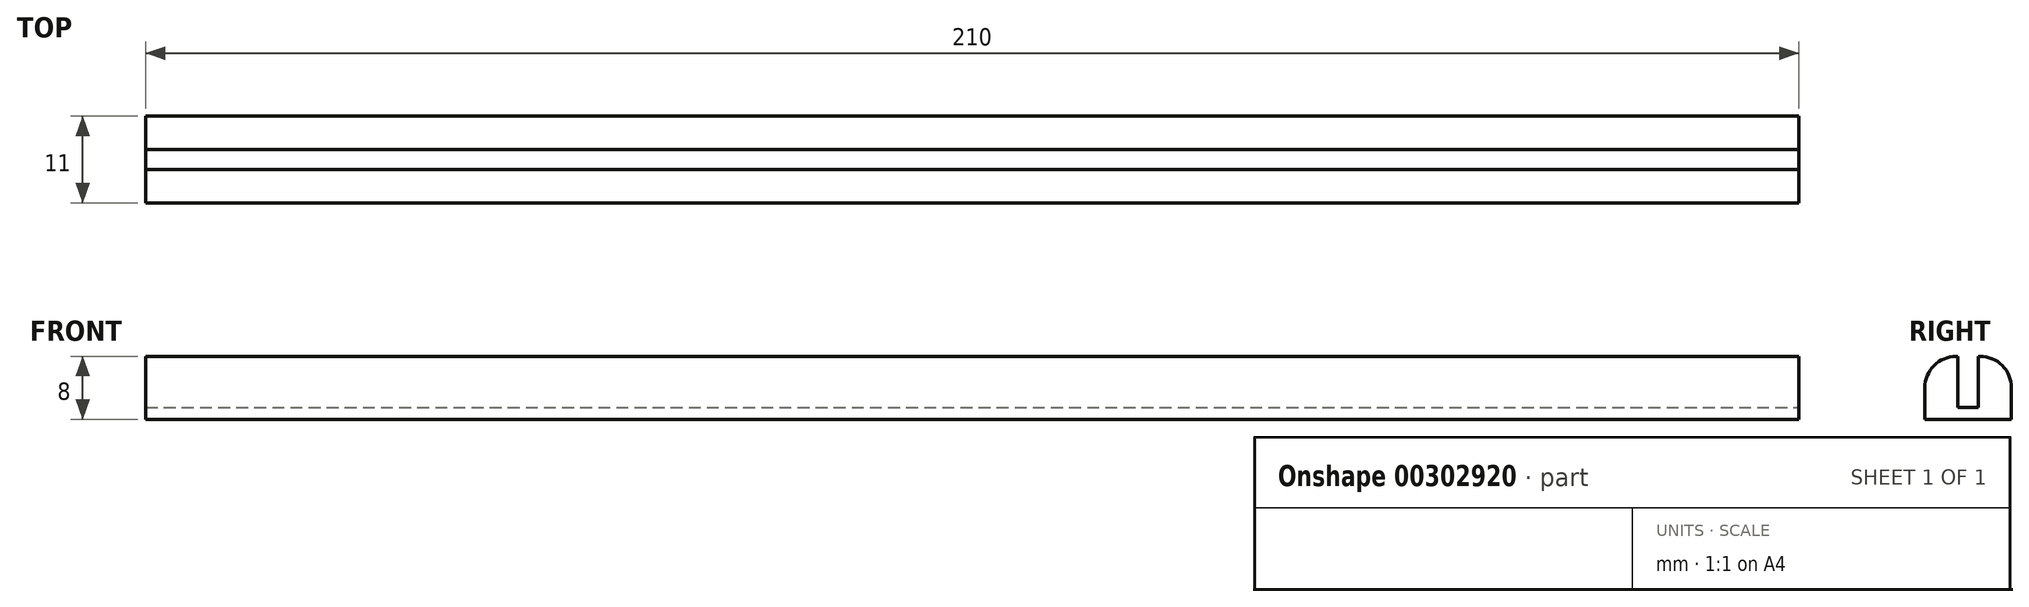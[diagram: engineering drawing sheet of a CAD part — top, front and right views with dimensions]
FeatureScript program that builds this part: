
annotation { "Feature Type Name" : "Feature", "Feature Type Description" : "" }
export const myFeature = defineFeature(function(context is Context, id is Id, definition is map)
    precondition{}
    {
        {
            var Q0;
            Q0=qCreatedBy(makeId("Top.planeOp"),FACE);
            var sketch = newSketch(context, id + "F0", { "sketchPlane" : qUnion([Q0])});
            skLineSegment(sketch, "E0.bottom", {"start": v(105, 5.5) * mm, "end": v(-105, 5.5) * mm});
            skLineSegment(sketch, "E0.top", {"start": v(105, -5.5) * mm, "end": v(-105, -5.5) * mm});
            skLineSegment(sketch, "E0.left", {"start": v(105, 5.5) * mm, "end": v(105, -5.5) * mm});
            skLineSegment(sketch, "E0.right", {"start": v(-105, 5.5) * mm, "end": v(-105, -5.5) * mm});
            skPoint(sketch, "E0.middle", {"position": v(0, 0) * mm});
            skLineSegment(sketch, "E1", {"start": v(-105, 1.3) * mm, "end": v(105, 1.3) * mm});
            skLineSegment(sketch, "E2", {"start": v(-105, -1.3) * mm, "end": v(105, -1.3) * mm});
            skSolve(sketch);
        }
        {
            var Q0;
            {var subQ0=sQuery(id+"F0.wireOp",EDGE,"E1");Q0=makeQuery(id+"F0.imprint","IMPRINT",FACE,{"disambiguationData":[TD([[makeQuery(id+"F0.imprint","IMPRINT",EDGE,{"derivedFrom":subQ0}),-1.0]])]});}
            extrude(context, id + "F1", {"entities" : qUnion([Q0]), "depth" : 1.5 * mm});
        }
        {
            var Q0;
            {var subQ0=sQuery(id+"F0.wireOp",EDGE,"E0.bottom");Q0=makeQuery(id+"F0.imprint","IMPRINT",FACE,{"disambiguationData":[TD([[makeQuery(id+"F0.imprint","IMPRINT",EDGE,{"derivedFrom":subQ0}),1.0]])]});}
            var Q1;
            {var subQ0=sQuery(id+"F0.wireOp",EDGE,"E0.top");Q1=makeQuery(id+"F0.imprint","IMPRINT",FACE,{"disambiguationData":[TD([[makeQuery(id+"F0.imprint","IMPRINT",EDGE,{"derivedFrom":subQ0}),-1.0]])]});}
            extrude(context, id + "F2", {"entities" : qUnion([Q0, Q1]), "operationType" : NewBodyOperationType.ADD, "depth" : 8 * mm});
        }
        {
            var Q0;
            Q0=makeQuery(id+"F2.opExtrude","CAP_EDGE",EDGE,{"disambiguationData":[OSD([sQuery(id+"F0.wireOp",EDGE,"E0.bottom")])],"isStart":false});
            var Q1;
            Q1=makeQuery(id+"F2.opExtrude","CAP_EDGE",EDGE,{"disambiguationData":[OSD([sQuery(id+"F0.wireOp",EDGE,"E0.top")])],"isStart":false});
            fillet(context, id + "F3", {"entities" : qUnion([Q0, Q1]), "radius" : 4 * mm, "tangentPropagation" : true, "allowEdgeOverflow" : false});
        }
    });
